# Revit family: Covrit Panel
name_source: partatom
category: Curtain Panels
revit_build: Autodesk Revit 2017 (Build: 20190508_0315(x64)
units: mm (PartAtom-declared; Revit-internal decimal feet)

## family parameters
Always vertical = Yes
Cut with Voids When Loaded = No
OmniClass Number = 23.25.20.14.11.11.17
OmniClass Title = Infill Panels
Shared = No

## types (7) — shared parameters
Analytic Construction = <None>
Assembly Code = G2040100
Bottom Rail Height = 0' - 1"
Bottom Rail Thickness = 0' - 2"
Brick Ledge Finish = <By Category>
Corr Panel Array Spacing = 0' - 6 3/4"
Description = Complete Enclosure System Product
Ground Offset = 0' - 4"
Ipe Max Height = 10' - 0"
Ipe Max Width = 6' - 6"
Ipe Thickness = 0' - 2 1/4"
Manufacturer = CityScapes, Inc.
Metal Series Max Height = 14' - 0"
Metal Series Max Width = 6' - 0"
Metal Series Thickness = 0' - 2 5/8"
Model = covRit - Screening Systems
Plankwall PVC Max Height = 12' - 0"
Plankwall PVC Max Width = 6' - 6"
Plankwall PVC Thickness = 0' - 1"
Rail Finish = <By Category>
Roman Ogee Rail = No
Type Comments = Enclosure Panels with Top & Bottom Rails
URL = www.cityscapesinc.com
Version = 191001

## per-type parameters (varying)
| type | Boxed Top Rail | Brick Panel Finish | IPE | Max Height | Max Width | NonMetal Series | Panel Finish | Panel Thickness | Plankwall Rail | Slat Size | Slat Spacing | Slats | Thickness | Top Rail Height | Top Rail Thickness | With Brick |
| Metal Series | Yes | <By Category> | No | 14' - 0" | 6' - 0" | No | <By Category> | 0' - 2 5/8" | No | 0' - 6" | 0' - 4" | No | 0' - 2 5/8" | 0' - 2 1/8" | 0' - 2 5/8" | No |
| Plankwall PVC | No | Covrit - Brick | No | 12' - 0" | 5' - 6" | Yes | Covrit - Panel Batten | 0' - 1" | Yes | 0' - 6" | 0' - 4" | No | 0' - 1" | 0' - 2" | 0' - 1" | Yes |
| Ipe | Yes | <By Category> | Yes | 9' - 6" | 6' - 3" | Yes | Covrit - IPE | 0' - 2 1/4" | No | 0' - 6" | 0' - 4" | No | 0' - 2 1/4" | 0' - 2" | 0' - 2 1/4" | No |
| Acrylicap ABS | Yes | <By Category> | No | 8' - 0" | 6' - 6" | Yes | Covrit - Panel Batten | 0' - 1 5/8" | No | 0' - 6" | 0' - 4" | No | 0' - 1 5/8" | 0' - 2" | 0' - 1 5/8" | No |
| Acrylicap ABS Clapboard | Yes | <By Category> | No | 8' - 0" | 6' - 6" | Yes | Covrit - Plank | 0' - 1 5/8" | No | 0' - 6" | 0' - 4" | No | 0' - 1 5/8" | 0' - 2" | 0' - 1 5/8" | No |
| 6" Slat Wall | Yes | <By Category> | No | 14' - 0" | 6' - 0" | No | <By Category> | 0' - 2 5/8" | No | 0' - 6" | 0' - 4" | Yes | 0' - 2 5/8" | 0' - 2 1/8" | 0' - 2 5/8" | No |
| 4" Slat Wall | Yes | <By Category> | No | 14' - 0" | 6' - 0" | No | <By Category> | 0' - 2 5/8" | No | 0' - 4" | 0' - 3" | Yes | 0' - 2 5/8" | 0' - 2" | 0' - 2 5/8" | No |

type visibility flags (boolean, named after types; folded from table):
- Metal Series: Yes: Metal Series
- Plankwall PVC: Yes: Plankwall PVC
- Ipe: Yes: (none)
- Acrylicap ABS: Yes: Acrylicap ABS
- Acrylicap ABS Clapboard: Yes: Acrylicap ABS
- 6" Slat Wall: Yes: 6" Slat Wall
- 4" Slat Wall: Yes: 4" Slat Wall

## geometry (parser evidence)
native form markers: Sweep x8
no freeform markers — native parametric forms only
